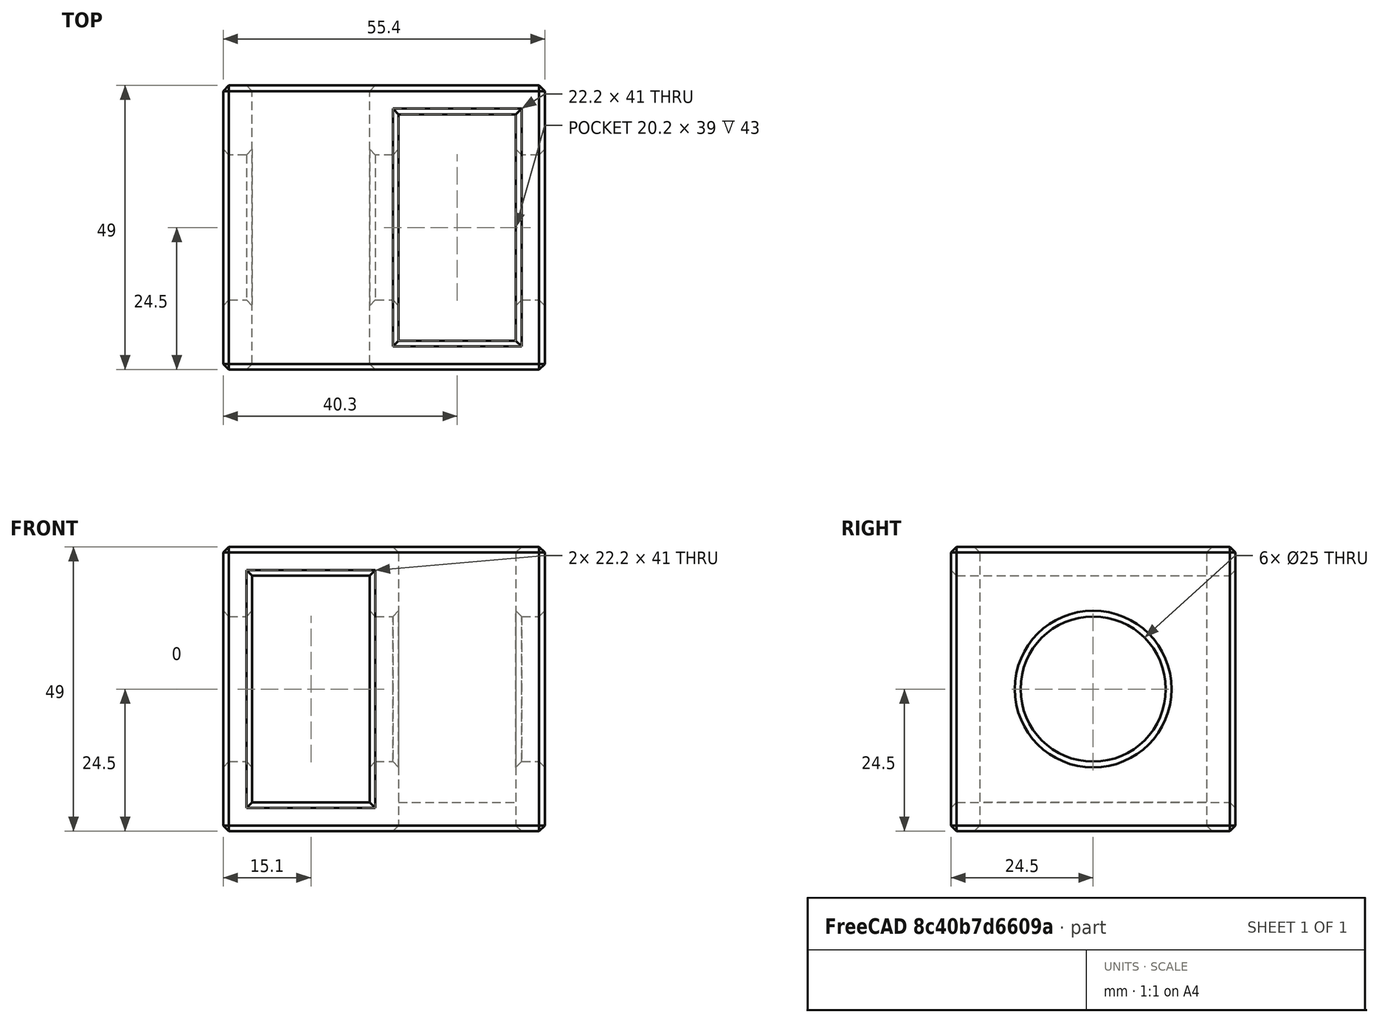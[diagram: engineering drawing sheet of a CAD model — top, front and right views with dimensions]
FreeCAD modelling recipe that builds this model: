
FCSTD DOCUMENT  (FreeCAD 0.21R33771 (Git))
Label: TargetStandBracket
License: All rights reserved
LicenseURL: http://en.wikipedia.org/wiki/All_rights_reserved
objects: Sketcher::SketchObject×8, PartDesign::Pocket×6, PartDesign::Pad×2, PartDesign::Chamfer×2, PartDesign::Body×2, Mesh::Feature×2, Spreadsheet::Sheet×1, App::Part×1
note: 30 computed .brp shape members not serialized (recipe doc carries the construction recipe); baked Part::Feature solids carry a one-line shape summary decoded from their .brp

FEATURE [Spreadsheet::Sheet] Spreadsheet  label="Parameters"
  cells = A2='Wood; B3='Wood_Wide; C3(Wood_Wide)=39; D3='mm; B4='Wood_Narrow; C4(Wood_Narrow)=20.2; D4='mm; A7='Bracket; B8='Bracket_Wall; C8(Bracket_Wall)=5; D8='mm; B9='Bracket_Width; C9(Bracket_Width)==C4 * 2 + C8 * 3; D9='mm; E9='calculated; B10='Bracket_Length; C10(Bracket_Length)==C3 + C8 * 2; D10='mm; E10='calculated; B11='Bracket_Height; C11(Bracket_Height)==C3 + C8 * 2; D11='mm; E11='calculated; B12='Bracket_Hole; C12(Bracket_Hole)=25; D12='mm
FEATURE [Sketcher::SketchObject] Sketch  label="Bracket-Sketch"
  FullyConstrained = true
  MapMode = 5
  Support = -> [XY_Plane001]
  expr: Constraints[10] = <<Parameters>>.Bracket_Length
  expr: Constraints[9] = <<Parameters>>.Bracket_Width
  sketch-geometry (4):
    g0: LineSegment StartX=-27.7 StartY=24.5 StartZ=0 EndX=27.7 EndY=24.5 EndZ=0
    g1: LineSegment StartX=27.7 StartY=24.5 StartZ=0 EndX=27.7 EndY=-24.5 EndZ=0
    g2: LineSegment StartX=27.7 StartY=-24.5 StartZ=0 EndX=-27.7 EndY=-24.5 EndZ=0
    g3: LineSegment StartX=-27.7 StartY=-24.5 StartZ=0 EndX=-27.7 EndY=24.5 EndZ=0
  constraints (11):
    c: Coincident(g0,g1)
    c: Coincident(g1,g2)
    c: Coincident(g2,g3)
    c: Coincident(g3,g0)
    c: Horizontal(g0)
    c: Horizontal(g2)
    c: Vertical(g1)
    c: Vertical(g3)
    c: Symmetric(g0,g2,g-1)
    c: DistanceX(g0,g0) = 55.4
    c: DistanceY(g1,g0) = 49
FEATURE [PartDesign::Pad] Pad  label="Bracket-Pad"
  Direction = (0,0,1)
  Length = 49
  Length2 = 10
  Midplane = true
  Profile = -> Sketch
  ReferenceAxis = -> Sketch [N_Axis]
  Type = 0
  expr: Length = <<Parameters>>.Bracket_Height
FEATURE [Sketcher::SketchObject] Sketch001  label="Slot_A-Sketch"
  AttachmentOffset = pos=(0,0,29.5) rot=(0,0,1;0rad)
  FullyConstrained = true
  MapMode = 5
  Placement = pos=(0,0,29.5) rot=(0,0,1;0rad)
  Support = -> [XY_Plane001]
  expr: .AttachmentOffset.Base.z = <<Parameters>>.Bracket_Height / 2 + <<Parameters>>.Bracket_Wall
  expr: Constraints[10] = <<Parameters>>.Wood_Narrow
  expr: Constraints[8] = <<Parameters>>.Bracket_Wall / 2
  expr: Constraints[9] = <<Parameters>>.Wood_Wide
  sketch-geometry (4):
    g0: LineSegment StartX=2.5 StartY=19.5 StartZ=0 EndX=22.7 EndY=19.5 EndZ=0
    g1: LineSegment StartX=22.7 StartY=19.5 StartZ=0 EndX=22.7 EndY=-19.5 EndZ=0
    g2: LineSegment StartX=22.7 StartY=-19.5 StartZ=0 EndX=2.5 EndY=-19.5 EndZ=0
    g3: LineSegment StartX=2.5 StartY=-19.5 StartZ=0 EndX=2.5 EndY=19.5 EndZ=0
  constraints (11):
    c: Coincident(g0,g1)
    c: Coincident(g1,g2)
    c: Coincident(g2,g3)
    c: Coincident(g3,g0)
    c: Horizontal(g0)
    c: Horizontal(g2)
    c: Vertical(g1)
    c: Symmetric(g0,g2,g-1)
    c: DistanceX(g-1,g0) = 2.5
    c: DistanceY(g1,g0) = 39
    c: DistanceX(g2,g1) = 20.2
FEATURE [PartDesign::Pocket] Pocket  label="Slot_A-Pocket"
  BaseFeature = -> Pad
  Direction = (0,0,-1)
  Length = 49
  Length2 = 5
  Profile = -> Sketch001
  ReferenceAxis = -> Sketch001 [N_Axis]
  Type = 0
  expr: Length = <<Parameters>>.Bracket_Height
FEATURE [Sketcher::SketchObject] Sketch002  label="Slot_B-Sketch"
  FullyConstrained = true
  MapMode = 5
  Placement = pos=(0,0,0) rot=(1,0,0;1.5708rad)
  Support = -> [XZ_Plane001]
  expr: Constraints[7] = <<Parameters>>.Bracket_Wall / 2
  expr: Constraints[8] = <<Parameters>>.Wood_Narrow
  expr: Constraints[9] = <<Parameters>>.Wood_Wide
  sketch-geometry (4):
    g0: LineSegment StartX=-22.7 StartY=19.5 StartZ=0 EndX=-2.5 EndY=19.5 EndZ=0
    g1: LineSegment StartX=-2.5 StartY=19.5 StartZ=0 EndX=-2.5 EndY=-19.5 EndZ=0
    g2: LineSegment StartX=-2.5 StartY=-19.5 StartZ=0 EndX=-22.7 EndY=-19.5 EndZ=0
    g3: LineSegment StartX=-22.7 StartY=-19.5 StartZ=0 EndX=-22.7 EndY=19.5 EndZ=0
  constraints (11):
    c: Coincident(g0,g1)
    c: Coincident(g1,g2)
    c: Coincident(g2,g3)
    c: Coincident(g3,g0)
    c: Horizontal(g0)
    c: Horizontal(g2)
    c: Vertical(g1)
    c: DistanceX(g0,g-1) = 2.5
    c: DistanceX(g0,g0) = 20.2
    c: DistanceY(g2,g0) = 39
    c: Symmetric(g0,g2,g-1)
FEATURE [PartDesign::Pocket] Pocket001  label="Slot_B-Pocket"
  BaseFeature = -> Pocket
  Direction = (0,1,2e-16)
  Length = 5
  Length2 = 5
  Midplane = true
  Profile = -> Sketch002
  ReferenceAxis = -> Sketch002 [N_Axis]
  Type = 1
FEATURE [Sketcher::SketchObject] Sketch003  label="Hole-Sketch"
  FullyConstrained = true
  MapMode = 5
  Placement = pos=(0,0,0) rot=(0.57735,0.57735,0.57735;2.0944rad)
  Support = -> [YZ_Plane001]
  expr: Constraints[1] = <<Parameters>>.Bracket_Hole
  sketch-geometry (1):
    g0: Circle CenterX=0 CenterY=0 CenterZ=0 NormalX=0 NormalY=0 NormalZ=1 AngleXU=0 Radius=12.5
  constraints (2):
    c: Coincident(g0,g-1)
    c: Diameter(g0) = 25
FEATURE [PartDesign::Pocket] Pocket002  label="Hole-Pocket"
  BaseFeature = -> Pocket001
  Direction = (-1,2e-16,-3e-16)
  Length = 5
  Length2 = 5
  Midplane = true
  Profile = -> Sketch003
  ReferenceAxis = -> Sketch003 [N_Axis]
  Type = 1
FEATURE [PartDesign::Chamfer] Chamfer
  Angle = 45
  Base = -> Pocket002 [Edge16,Edge9,Edge14,Edge27,Edge29,Edge32,Edge23,Edge21,Edge15,Edge22,Edge13,Edge4,Edge19,Edge18,Edge17,Edge20,Edge11,Edge3,Edge37,Edge42,Edge2,Edge5,Edge6,Edge7,Edge8,Edge1,Edge10,Edge12,Edge31,Edge26]
  BaseFeature = -> Pocket002
  ChamferType = 0
  FlipDirection = false
  Size = 1
  Size2 = 1
  SupportTransform = false
  UseAllEdges = false
FEATURE [PartDesign::Body] Body  label="Capped-Body"
  Group = -> [Sketch,Pad,Sketch001,Pocket,Sketch002,Pocket001,Sketch003,Pocket002,Chamfer]
  Origin = -> Origin001
  Tip = -> Chamfer
FEATURE [Sketcher::SketchObject] Sketch004  label="Bracket-Sketch001"
  FullyConstrained = true
  MapMode = 5
  Support = -> [XY_Plane002]
  expr: Constraints[10] = <<Parameters>>.Bracket_Length
  expr: Constraints[9] = <<Parameters>>.Bracket_Width
  sketch-geometry (4):
    g0: LineSegment StartX=-27.7 StartY=24.5 StartZ=0 EndX=27.7 EndY=24.5 EndZ=0
    g1: LineSegment StartX=27.7 StartY=24.5 StartZ=0 EndX=27.7 EndY=-24.5 EndZ=0
    g2: LineSegment StartX=27.7 StartY=-24.5 StartZ=0 EndX=-27.7 EndY=-24.5 EndZ=0
    g3: LineSegment StartX=-27.7 StartY=-24.5 StartZ=0 EndX=-27.7 EndY=24.5 EndZ=0
  constraints (11):
    c: Coincident(g0,g1)
    c: Coincident(g1,g2)
    c: Coincident(g2,g3)
    c: Coincident(g3,g0)
    c: Horizontal(g0)
    c: Horizontal(g2)
    c: Vertical(g1)
    c: Vertical(g3)
    c: Symmetric(g0,g2,g-1)
    c: DistanceX(g0,g0) = 55.4
    c: DistanceY(g1,g0) = 49
FEATURE [PartDesign::Pad] Pad001  label="Bracket-Pad001"
  Direction = (0,0,1)
  Length = 49
  Length2 = 10
  Midplane = true
  Profile = -> Sketch004
  ReferenceAxis = -> Sketch004 [N_Axis]
  Type = 0
  expr: Length = <<Parameters>>.Bracket_Height
FEATURE [Sketcher::SketchObject] Sketch005  label="Slot_A-Sketch001"
  FullyConstrained = true
  MapMode = 5
  Support = -> [XY_Plane002]
  expr: Constraints[10] = <<Parameters>>.Wood_Narrow
  expr: Constraints[8] = <<Parameters>>.Bracket_Wall / 2
  expr: Constraints[9] = <<Parameters>>.Wood_Wide
  sketch-geometry (4):
    g0: LineSegment StartX=2.5 StartY=19.5 StartZ=0 EndX=22.7 EndY=19.5 EndZ=0
    g1: LineSegment StartX=22.7 StartY=19.5 StartZ=0 EndX=22.7 EndY=-19.5 EndZ=0
    g2: LineSegment StartX=22.7 StartY=-19.5 StartZ=0 EndX=2.5 EndY=-19.5 EndZ=0
    g3: LineSegment StartX=2.5 StartY=-19.5 StartZ=0 EndX=2.5 EndY=19.5 EndZ=0
  constraints (11):
    c: Coincident(g0,g1)
    c: Coincident(g1,g2)
    c: Coincident(g2,g3)
    c: Coincident(g3,g0)
    c: Horizontal(g0)
    c: Horizontal(g2)
    c: Vertical(g1)
    c: Symmetric(g0,g2,g-1)
    c: DistanceX(g-1,g0) = 2.5
    c: DistanceY(g1,g0) = 39
    c: DistanceX(g2,g1) = 20.2
FEATURE [PartDesign::Pocket] Pocket003  label="Slot_A-Pocket001"
  BaseFeature = -> Pad001
  Direction = (0,0,-1)
  Length = 5
  Length2 = 5
  Midplane = true
  Profile = -> Sketch005
  ReferenceAxis = -> Sketch005 [N_Axis]
  Type = 1
FEATURE [Sketcher::SketchObject] Sketch006  label="Slot_B-Sketch001"
  FullyConstrained = true
  MapMode = 5
  Placement = pos=(0,0,0) rot=(1,0,0;1.5708rad)
  Support = -> [XZ_Plane002]
  expr: Constraints[7] = <<Parameters>>.Bracket_Wall / 2
  expr: Constraints[8] = <<Parameters>>.Wood_Narrow
  expr: Constraints[9] = <<Parameters>>.Wood_Wide
  sketch-geometry (4):
    g0: LineSegment StartX=-22.7 StartY=19.5 StartZ=0 EndX=-2.5 EndY=19.5 EndZ=0
    g1: LineSegment StartX=-2.5 StartY=19.5 StartZ=0 EndX=-2.5 EndY=-19.5 EndZ=0
    g2: LineSegment StartX=-2.5 StartY=-19.5 StartZ=0 EndX=-22.7 EndY=-19.5 EndZ=0
    g3: LineSegment StartX=-22.7 StartY=-19.5 StartZ=0 EndX=-22.7 EndY=19.5 EndZ=0
  constraints (11):
    c: Coincident(g0,g1)
    c: Coincident(g1,g2)
    c: Coincident(g2,g3)
    c: Coincident(g3,g0)
    c: Horizontal(g0)
    c: Horizontal(g2)
    c: Vertical(g1)
    c: DistanceX(g0,g-1) = 2.5
    c: DistanceX(g0,g0) = 20.2
    c: DistanceY(g2,g0) = 39
    c: Symmetric(g0,g2,g-1)
FEATURE [PartDesign::Pocket] Pocket004  label="Slot_B-Pocket001"
  BaseFeature = -> Pocket003
  Direction = (0,1,2e-16)
  Length = 5
  Length2 = 5
  Midplane = true
  Profile = -> Sketch006
  ReferenceAxis = -> Sketch006 [N_Axis]
  Type = 1
FEATURE [Sketcher::SketchObject] Sketch007  label="Hole-Sketch001"
  FullyConstrained = true
  MapMode = 5
  Placement = pos=(0,0,0) rot=(0.57735,0.57735,0.57735;2.0944rad)
  Support = -> [YZ_Plane002]
  expr: Constraints[1] = <<Parameters>>.Bracket_Hole
  sketch-geometry (1):
    g0: Circle CenterX=0 CenterY=0 CenterZ=0 NormalX=0 NormalY=0 NormalZ=1 AngleXU=0 Radius=12.5
  constraints (2):
    c: Coincident(g0,g-1)
    c: Diameter(g0) = 25
FEATURE [PartDesign::Pocket] Pocket005  label="Hole-Pocket001"
  BaseFeature = -> Pocket004
  Direction = (-1,2e-16,-3e-16)
  Length = 5
  Length2 = 5
  Midplane = true
  Profile = -> Sketch007
  ReferenceAxis = -> Sketch007 [N_Axis]
  Type = 1
FEATURE [PartDesign::Chamfer] Chamfer001
  Angle = 45
  Base = -> Pocket005 [Edge9,Edge20,Edge14,Edge25,Edge19,Edge11,Edge3,Edge4,Edge13,Edge26,Edge43,Edge40,Edge21,Edge22,Edge23,Edge24,Edge36,Edge33,Edge31,Edge27,Edge35,Edge12,Edge30,Edge2,Edge1,Edge7,Edge5,Edge8,Edge6,Edge10,Edge15,Edge16,Edge18,Edge17]
  BaseFeature = -> Pocket005
  ChamferType = 0
  FlipDirection = false
  Size = 1
  Size2 = 1
  SupportTransform = false
  UseAllEdges = false
FEATURE [PartDesign::Body] Body001  label="Normal-Body"
  Group = -> [Sketch004,Pad001,Sketch005,Pocket003,Sketch006,Pocket004,Sketch007,Pocket005,Chamfer001]
  Origin = -> Origin002
  Tip = -> Chamfer001
FEATURE [App::Part] Part
  Group = -> [Spreadsheet,Body,Body001]
  Origin = -> Origin
FEATURE [Mesh::Feature] Mesh  label="Chamfer (Meshed)"
FEATURE [Mesh::Feature] Mesh001  label="Chamfer001 (Meshed)"
